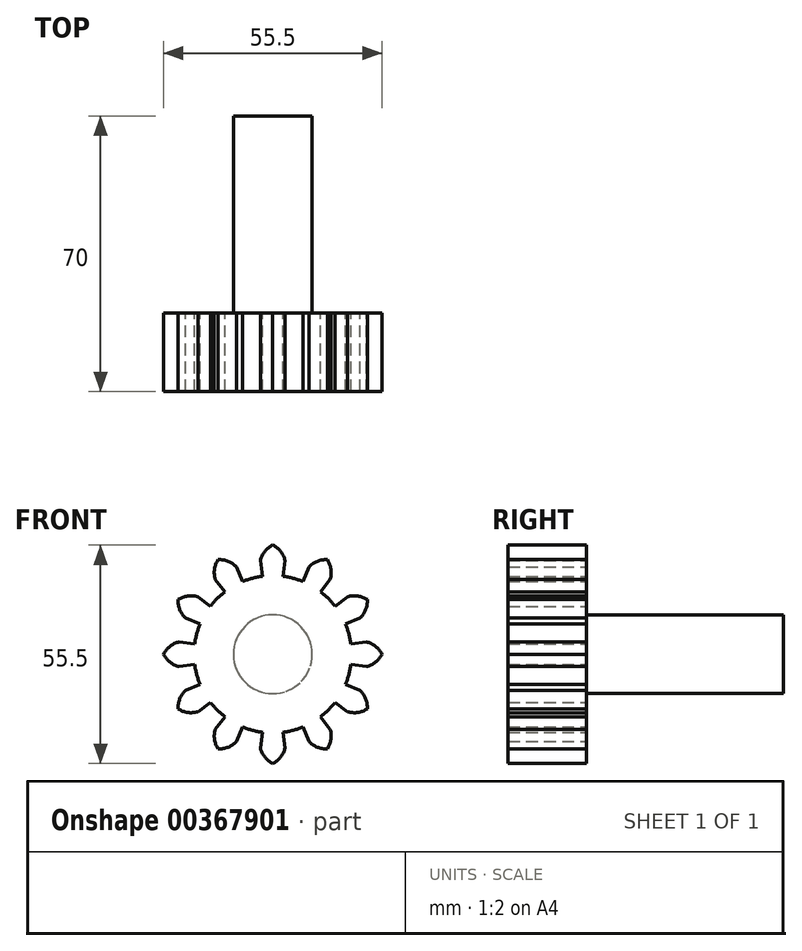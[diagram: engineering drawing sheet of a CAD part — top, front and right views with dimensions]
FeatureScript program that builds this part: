
annotation { "Feature Type Name" : "Feature", "Feature Type Description" : "" }
export const myFeature = defineFeature(function(context is Context, id is Id, definition is map)
    precondition{}
    {
        {
            assignVariable(context, id + "F0", {"name" : "N", "anyValue" : 12});
        }
        {
            var Q0;
            Q0=qCreatedBy(makeId("Front.planeOp"),FACE);
            var sketch = newSketch(context, id + "F1", { "sketchPlane" : qUnion([Q0])});
            skCircle(sketch, "E0", {"center": v(0, 0) * mm, "radius": 20 * mm});
            skCircle(sketch, "E1", {"center": v(0, 0) * mm, "radius": 24 * mm, "construction": true});
            skCircle(sketch, "E2", {"center": v(0, 0) * mm, "radius": 28 * mm, "construction": true});
            skLineSegment(sketch, "E3", {"start": v(3.13, 23.8) * mm, "end": v(-53.59, 31.26) * mm, "construction": true});
            skLineSegment(sketch, "E4", {"start": v(-55.6, 10.77) * mm, "end": v(3.13, 23.8) * mm, "construction": true});
            skCircle(sketch, "E5", {"center": v(0, 0) * mm, "radius": 22.55 * mm, "construction": true});
            skCircle(sketch, "E6", {"center": v(3.13, 23.8) * mm, "radius": 6 * mm, "construction": true});
            skCircle(sketch, "E7", {"center": v(-2.7, 22.4) * mm, "radius": 6 * mm, "construction": true});
            skLineSegment(sketch, "E8", {"start": v(0, 0) * mm, "end": v(-11.02, 83.68) * mm, "construction": true});
            skLineSegment(sketch, "E9", {"start": v(-11.02, 83.68) * mm, "end": v(11.02, 83.68) * mm, "construction": true});
            skLineSegment(sketch, "E10", {"start": v(11.02, 83.68) * mm, "end": v(0, 0) * mm, "construction": true});
            skLineSegment(sketch, "E11", {"start": v(0, 0) * mm, "end": v(0, 83.68) * mm, "construction": true});
            skLineSegment(sketch, "E12", {"start": v(2.61, 19.83) * mm, "end": v(3.13, 23.8) * mm});
            skArc(sketch, "E13", {"start": v(3.13, 23.8) * mm, "mid": v(1.8, 26.35) * mm, "end": v(-0.56, 28) * mm});
            skArc(sketch, "E14", {"start": v(-0.56, 28) * mm, "mid": v(0.28, -28) * mm, "end": v(0, 28) * mm});
            skLineSegment(sketch, "E15.MirrorCS", {"start": v(-2.61, 19.83) * mm, "end": v(-3.13, 23.8) * mm});
            skArc(sketch, "E16.MirrorCS", {"start": v(-3.13, 23.8) * mm, "mid": v(-1.8, 26.35) * mm, "end": v(0.56, 28) * mm});
            skArc(sketch, "E17.MirrorCS", {"start": v(0.56, 28) * mm, "mid": v(-0.28, -28) * mm, "end": v(0, 28) * mm});
            skSolve(sketch);
        }
        {
            var Q0;
            {var subQ0=sQuery(id+"F1.wireOp",EDGE,"E0");var subQ1=makeQuery(id+"F1.imprint","INTERSECT",VERTEX,{"derivedFrom":[subQ0,sQuery(id+"F1.wireOp",EDGE,"E12")]});Q0=makeQuery(id+"F1.imprint","IMPRINT",FACE,{"disambiguationData":[TD([[makeQuery(id+"F1.imprint","IMPRINT",EDGE,{"disambiguationData":[TD([[subQ1,-1.0]])],"derivedFrom":subQ0}),1.0]])]});}
            var Q1;
            {var subQ0=sQuery(id+"F1.wireOp",EDGE,"E12");Q1=makeQuery(id+"F1.imprint","IMPRINT",FACE,{"disambiguationData":[TD([[makeQuery(id+"F1.imprint","IMPRINT",EDGE,{"derivedFrom":subQ0}),1.0]])]});}
            extrude(context, id + "F2", {"entities" : qUnion([Q0, Q1]), "endBound" : BoundingType.SYMMETRIC, "depth" : 20 * mm});
        }
        {
            var Q0;
            Q0=makeQuery(id+"F2.opExtrude","SWEPT_FACE",FACE,{"disambiguationData":[OSD([sQuery(id+"F1.wireOp",EDGE,"E15.MirrorCS")])]});
            var Q1;
            Q1=makeQuery(id+"F2.opExtrude","SWEPT_FACE",FACE,{"disambiguationData":[OSD([sQuery(id+"F1.wireOp",EDGE,"E16.MirrorCS")])]});
            var Q2;
            Q2=makeQuery(id+"F2.opExtrude","SWEPT_FACE",FACE,{"disambiguationData":[OSD([sQuery(id+"F1.wireOp",EDGE,"E14"),sQuery(id+"F1.wireOp",EDGE,"E17.MirrorCS")])]});
            var Q3;
            Q3=makeQuery(id+"F2.opExtrude","SWEPT_FACE",FACE,{"disambiguationData":[OSD([sQuery(id+"F1.wireOp",EDGE,"E13")])]});
            var Q4;
            Q4=makeQuery(id+"F2.opExtrude","SWEPT_FACE",FACE,{"disambiguationData":[OSD([sQuery(id+"F1.wireOp",EDGE,"E12")])]});
            var Q5;
            Q5=makeQuery(id+"F2.opExtrude","SWEPT_FACE",FACE,{"disambiguationData":[OSD([sQuery(id+"F1.wireOp",EDGE,"E0")])]});
            circularPattern(context, id + "F3", {"patternType" : PatternType.FACE, "faces" : qUnion([Q0, Q1, Q2, Q3, Q4]), "axis" : qUnion([Q5]), "angle" : 360 * degree, "instanceCount" : getVariable(context, 'N'), "equalSpace" : true});
        }
        {
            var Q0;
            Q0=makeQuery(id+"F2.opExtrude","CAP_FACE",FACE,{"disambiguationData":[OSD([sQuery(id+"F1.wireOp",EDGE,"E0"),sQuery(id+"F1.wireOp",EDGE,"E12"),sQuery(id+"F1.wireOp",EDGE,"E13"),sQuery(id+"F1.wireOp",EDGE,"E15.MirrorCS"),sQuery(id+"F1.wireOp",EDGE,"E16.MirrorCS")])],"isStart":true});
            var sketch = newSketch(context, id + "F4", { "sketchPlane" : qUnion([Q0])});
            skCircle(sketch, "E18", {"center": v(0, 0) * mm, "radius": 10 * mm});
            skSolve(sketch);
        }
        {
            var Q0;
            Q0=makeQuery(id+"F4.imprint","IMPRINT",FACE,{"disambiguationData":[TD([[makeQuery(id+"F4.imprint","IMPRINT",EDGE,{"derivedFrom":sQuery(id+"F4.wireOp",EDGE,"E18")}),1.0]])]});
            extrude(context, id + "F5", {"entities" : qUnion([Q0]), "operationType" : NewBodyOperationType.ADD, "depth" : 50 * mm});
        }
    });
